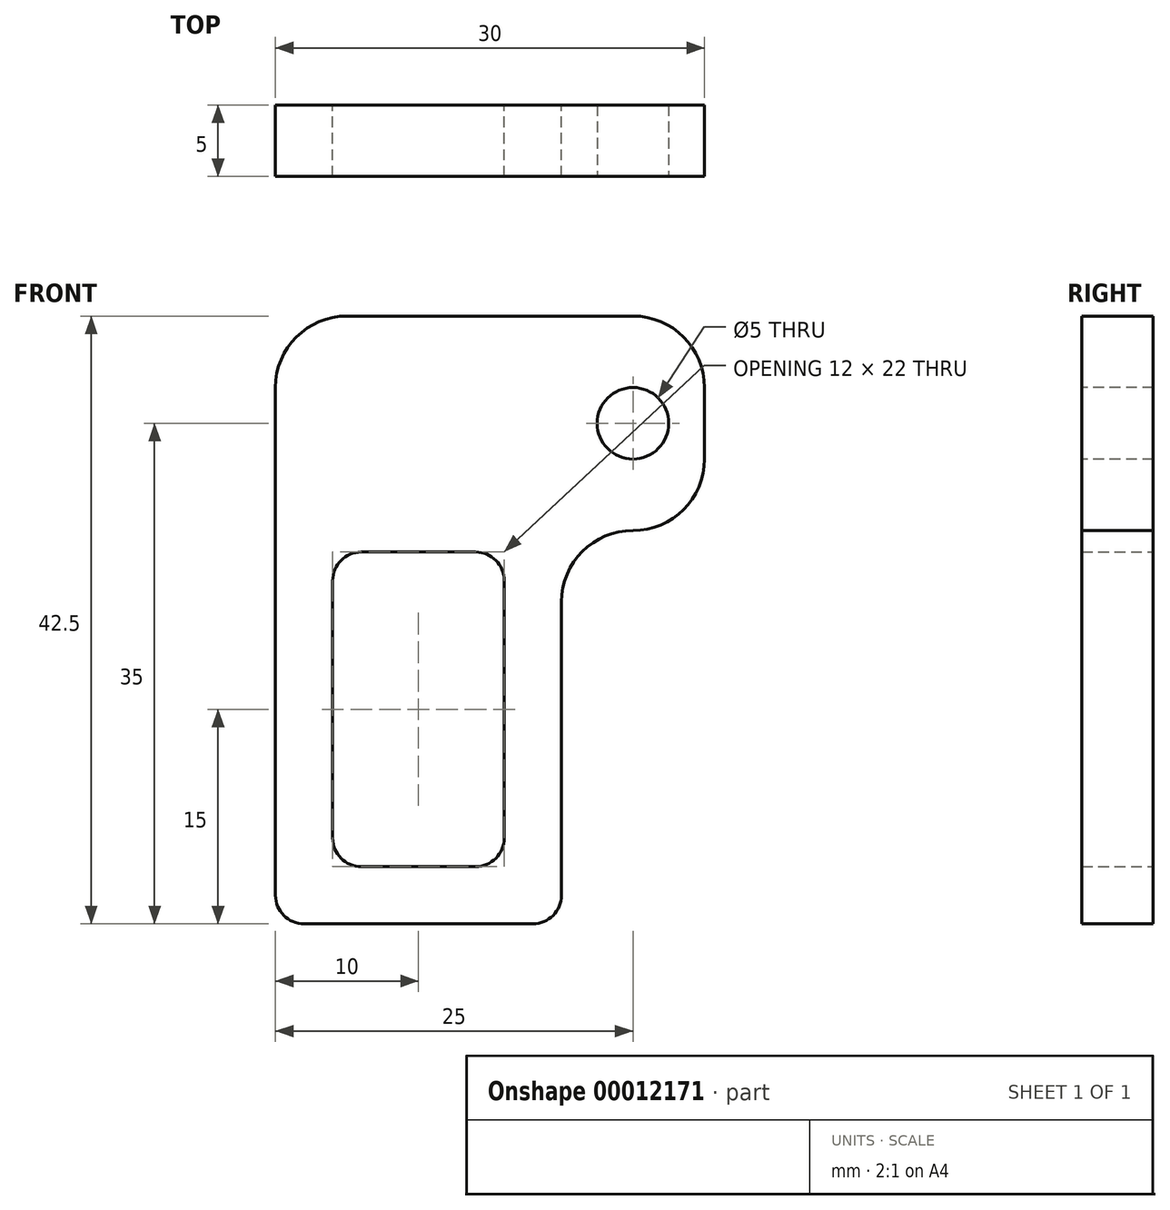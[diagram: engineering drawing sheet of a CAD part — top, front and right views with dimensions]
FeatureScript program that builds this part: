
annotation { "Feature Type Name" : "Feature", "Feature Type Description" : "" }
export const myFeature = defineFeature(function(context is Context, id is Id, definition is map)
    precondition{}
    {
        {
            var Q0;
            Q0=qCreatedBy(makeId("Front.planeOp"),FACE);
            var sketch = newSketch(context, id + "F0", { "sketchPlane" : qUnion([Q0])});
            skLineSegment(sketch, "E0.rect.bottom", {"start": v(10, -15) * mm, "end": v(-10, -15) * mm});
            skLineSegment(sketch, "E0.rect.top", {"start": v(10, 15) * mm, "end": v(-10, 15) * mm});
            skLineSegment(sketch, "E0.rect.left", {"start": v(10, -15) * mm, "end": v(10, 15) * mm});
            skLineSegment(sketch, "E0.rect.right", {"start": v(-10, -15) * mm, "end": v(-10, 15) * mm});
            skPoint(sketch, "E0.rect.middle", {"position": v(0, 0) * mm});
            skLineSegment(sketch, "E1", {"start": v(0, 15) * mm, "end": v(0, 20) * mm, "construction": true});
            skLineSegment(sketch, "E2.rect.bottom", {"start": v(20, 12.5) * mm, "end": v(-10, 12.5) * mm});
            skLineSegment(sketch, "E2.rect.top", {"start": v(20, 27.5) * mm, "end": v(-10, 27.5) * mm});
            skLineSegment(sketch, "E2.rect.left", {"start": v(20, 12.5) * mm, "end": v(20, 27.5) * mm});
            skPoint(sketch, "E2.rect.middle", {"position": v(0, 20) * mm});
            skLineSegment(sketch, "E3.rect.bottom", {"start": v(6, -11) * mm, "end": v(-6, -11) * mm});
            skLineSegment(sketch, "E3.rect.top", {"start": v(6, 11) * mm, "end": v(-6, 11) * mm});
            skLineSegment(sketch, "E3.rect.left", {"start": v(6, -11) * mm, "end": v(6, 11) * mm});
            skLineSegment(sketch, "E3.rect.right", {"start": v(-6, -11) * mm, "end": v(-6, 11) * mm});
            skLineSegment(sketch, "E4", {"start": v(-10, 15) * mm, "end": v(-10, 27.5) * mm});
            skSolve(sketch);
        }
        {
            var Q0;
            Q0=makeQuery(id+"F0.imprint","IMPRINT",FACE,{"disambiguationData":[TD([[makeQuery(id+"F0.imprint","IMPRINT",EDGE,{"derivedFrom":sQuery(id+"F0.wireOp",EDGE,"E2.rect.top")}),1.0]])]});
            var Q1;
            Q1=makeQuery(id+"F0.imprint","IMPRINT",FACE,{"disambiguationData":[TD([[makeQuery(id+"F0.imprint","IMPRINT",EDGE,{"derivedFrom":sQuery(id+"F0.wireOp",EDGE,"E0.rect.bottom")}),-1.0]])]});
            var Q2;
            {var subQ5=sQuery(id+"F0.wireOp",EDGE,"E0.rect.top");Q2=makeQuery(id+"F0.imprint","IMPRINT",FACE,{"disambiguationData":[TD([[makeQuery(id+"F0.imprint","IMPRINT",EDGE,{"derivedFrom":subQ5}),1.0]])]});}
            extrude(context, id + "F1", {"entities" : qUnion([Q0, Q1, Q2]), "depth" : 5 * mm});
        }
        {
            var Q0;
            Q0=makeQuery(id+"F1.opExtrude","SWEPT_EDGE",EDGE,{"disambiguationData":[OSD([sQuery(id+"F0.wireOp",EDGE,"E2.rect.top"),sQuery(id+"F0.wireOp",EDGE,"E2.rect.left")])]});
            var Q1;
            Q1=makeQuery(id+"F1.opExtrude","SWEPT_EDGE",EDGE,{"disambiguationData":[OSD([sQuery(id+"F0.wireOp",EDGE,"E2.rect.top"),sQuery(id+"F0.wireOp",EDGE,"E2.rect.right")])]});
            var Q2;
            Q2=makeQuery(id+"F1.opExtrude","SWEPT_EDGE",EDGE,{"disambiguationData":[OSD([sQuery(id+"F0.wireOp",EDGE,"E2.rect.bottom"),sQuery(id+"F0.wireOp",EDGE,"E2.rect.right")])]});
            var Q3;
            Q3=makeQuery(id+"F1.opExtrude","SWEPT_EDGE",EDGE,{"disambiguationData":[OSD([sQuery(id+"F0.wireOp",EDGE,"E2.rect.bottom"),sQuery(id+"F0.wireOp",EDGE,"E2.rect.left")])]});
            fillet(context, id + "F2", {"entities" : qUnion([Q0, Q1, Q2, Q3]), "radius" : 5 * mm, "tangentPropagation" : true, "allowEdgeOverflow" : false});
        }
        {
            var Q0;
            Q0=makeQuery(id+"F1.opExtrude","SWEPT_EDGE",EDGE,{"disambiguationData":[OSD([sQuery(id+"F0.wireOp",EDGE,"E0.rect.bottom"),sQuery(id+"F0.wireOp",EDGE,"E0.rect.left")])]});
            var Q1;
            Q1=makeQuery(id+"F1.opExtrude","SWEPT_EDGE",EDGE,{"disambiguationData":[OSD([sQuery(id+"F0.wireOp",EDGE,"E0.rect.bottom"),sQuery(id+"F0.wireOp",EDGE,"E0.rect.right")])]});
            var Q2;
            Q2=makeQuery(id+"F1.opExtrude","SWEPT_EDGE",EDGE,{"disambiguationData":[OSD([sQuery(id+"F0.wireOp",EDGE,"E3.rect.top"),sQuery(id+"F0.wireOp",EDGE,"E3.rect.left")])]});
            var Q3;
            Q3=makeQuery(id+"F1.opExtrude","SWEPT_EDGE",EDGE,{"disambiguationData":[OSD([sQuery(id+"F0.wireOp",EDGE,"E3.rect.top"),sQuery(id+"F0.wireOp",EDGE,"E3.rect.right")])]});
            var Q4;
            Q4=makeQuery(id+"F1.opExtrude","SWEPT_EDGE",EDGE,{"disambiguationData":[OSD([sQuery(id+"F0.wireOp",EDGE,"E3.rect.bottom"),sQuery(id+"F0.wireOp",EDGE,"E3.rect.left")])]});
            var Q5;
            Q5=makeQuery(id+"F1.opExtrude","SWEPT_EDGE",EDGE,{"disambiguationData":[OSD([sQuery(id+"F0.wireOp",EDGE,"E3.rect.bottom"),sQuery(id+"F0.wireOp",EDGE,"E3.rect.right")])]});
            fillet(context, id + "F3", {"entities" : qUnion([Q0, Q1, Q2, Q3, Q4, Q5]), "radius" : 2 * mm, "tangentPropagation" : true, "allowEdgeOverflow" : false});
        }
        {
            var Q0;
            Q0=makeQuery(id+"F1.opExtrude","CAP_FACE",FACE,{"disambiguationData":[OSD([sQuery(id+"F0.wireOp",EDGE,"E0.rect.bottom"),sQuery(id+"F0.wireOp",EDGE,"E0.rect.left"),sQuery(id+"F0.wireOp",EDGE,"E0.rect.right"),sQuery(id+"F0.wireOp",EDGE,"E2.rect.bottom"),sQuery(id+"F0.wireOp",EDGE,"E2.rect.top"),sQuery(id+"F0.wireOp",EDGE,"E2.rect.left"),sQuery(id+"F0.wireOp",EDGE,"E2.rect.right"),sQuery(id+"F0.wireOp",EDGE,"E3.rect.bottom"),sQuery(id+"F0.wireOp",EDGE,"E3.rect.top"),sQuery(id+"F0.wireOp",EDGE,"E3.rect.left"),sQuery(id+"F0.wireOp",EDGE,"E3.rect.right")])],"isStart":false});
            var sketch = newSketch(context, id + "F4", { "sketchPlane" : qUnion([Q0])});
            skCircle(sketch, "E5", {"center": v(15, 20) * mm, "radius": 2.5 * mm});
            skLineSegment(sketch, "E6", {"start": v(20, 20) * mm, "end": v(15, 20) * mm});
            skSolve(sketch);
        }
        {
            var Q0;
            Q0=makeQuery(id+"F4.imprint","IMPRINT",FACE,{"disambiguationData":[TD([[makeQuery(id+"F4.imprint","IMPRINT",EDGE,{"derivedFrom":sQuery(id+"F4.wireOp",EDGE,"E5")}),1.0]])]});
            var Q1;
            Q1=sQuery(id+"F4.wireOp",EDGE,"E5");
            extrude(context, id + "F5", {"entities" : qUnion([Q0]), "operationType" : NewBodyOperationType.REMOVE, "surfaceEntities" : qUnion([Q1]), "endBound" : BoundingType.THROUGH_ALL, "oppositeDirection" : true, "depth" : 25 * mm});
        }
    });
